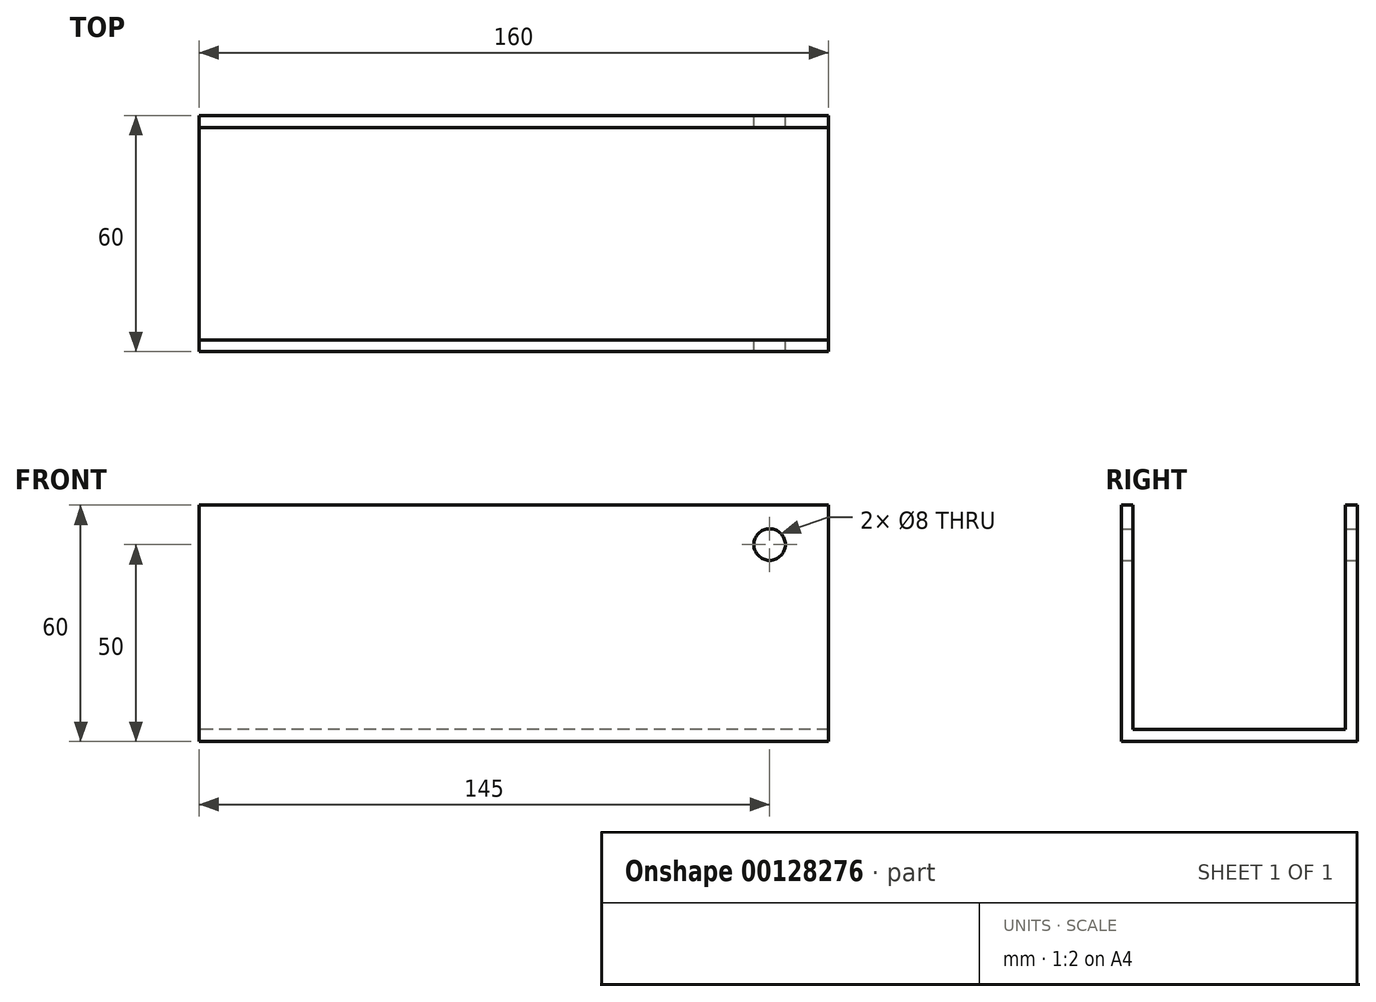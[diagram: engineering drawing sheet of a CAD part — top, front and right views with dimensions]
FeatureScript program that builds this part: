
annotation { "Feature Type Name" : "Feature", "Feature Type Description" : "" }
export const myFeature = defineFeature(function(context is Context, id is Id, definition is map)
    precondition{}
    {
        {
            var Q0;
            Q0=qCreatedBy(makeId("Right.planeOp"),FACE);
            var sketch = newSketch(context, id + "F0", { "sketchPlane" : qUnion([Q0])});
            skLineSegment(sketch, "E0.bottom", {"start": v(-30, -30) * mm, "end": v(30, -30) * mm});
            skLineSegment(sketch, "E0.top", {"start": v(-30, 30) * mm, "end": v(-27, 30) * mm});
            skLineSegment(sketch, "E0.left", {"start": v(-30, -30) * mm, "end": v(-30, 30) * mm});
            skLineSegment(sketch, "E0.right", {"start": v(30, -30) * mm, "end": v(30, 30) * mm});
            skPoint(sketch, "E0.middle", {"position": v(0, 0) * mm});
            skLineSegment(sketch, "E1.0", {"start": v(-27, -27) * mm, "end": v(-27, 30) * mm});
            skLineSegment(sketch, "E2.0", {"start": v(-27, -27) * mm, "end": v(27, -27) * mm});
            skLineSegment(sketch, "E3.0", {"start": v(27, -27) * mm, "end": v(27, 30) * mm});
            skLineSegment(sketch, "E4.trimOffspring", {"start": v(27, 30) * mm, "end": v(30, 30) * mm});
            skSolve(sketch);
        }
        {
            var Q0;
            Q0 = qSketchRegion(id + "F0", true);
            extrude(context, id + "F1", {"entities" : qUnion([Q0]), "depth" : 160 * mm});
        }
        {
            var Q0;
            Q0=makeQuery(id+"F1.opExtrude","SWEPT_FACE",FACE,{"disambiguationData":[OSD([sQuery(id+"F0.wireOp",EDGE,"E0.right")])]});
            var sketch = newSketch(context, id + "F2", { "sketchPlane" : qUnion([Q0])});
            skCircle(sketch, "E5", {"center": v(-145, 20) * mm, "radius": 4 * mm});
            skSolve(sketch);
        }
        {
            var Q0;
            Q0 = qSketchRegion(id + "F2", true);
            extrude(context, id + "F3", {"entities" : qUnion([Q0]), "operationType" : NewBodyOperationType.REMOVE, "endBound" : BoundingType.THROUGH_ALL, "oppositeDirection" : true, "depth" : 25 * mm});
        }
    });
